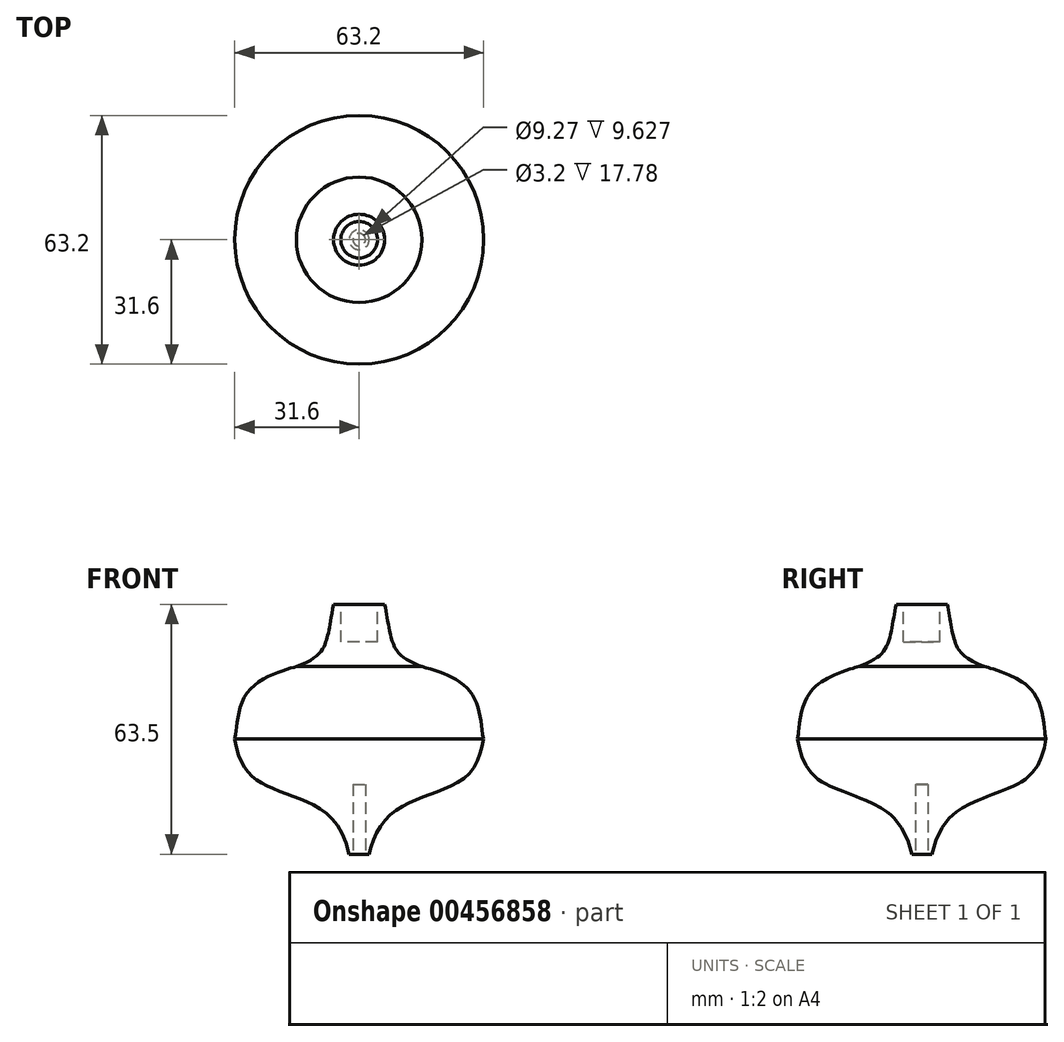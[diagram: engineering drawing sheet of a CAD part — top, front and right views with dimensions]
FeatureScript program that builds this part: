
annotation { "Feature Type Name" : "Feature", "Feature Type Description" : "" }
export const myFeature = defineFeature(function(context is Context, id is Id, definition is map)
    precondition{}
    {
        {
            var Q0;
            Q0=qCreatedBy(makeId("Front.planeOp"),FACE);
            var sketch = newSketch(context, id + "F0", { "sketchPlane" : qUnion([Q0])});
            skLineSegment(sketch, "E0", {"start": v(0, 0) * mm, "end": v(0, 63.5) * mm});
            skLineSegment(sketch, "E1", {"start": v(0, 63.5) * mm, "end": v(6.48, 63.5) * mm});
            skFitSpline(sketch, "E2", {"points": [v(6.48, 63.5) * mm, v(8.36, 54.25) * mm, v(15.93, 47.67) * mm], "startDerivative": vector(5.78, -29.87) * mm, "endDerivative": vector(33.4, -11.93) * mm});
            skLineSegment(sketch, "E3", {"start": v(0, 0) * mm, "end": v(2.54, 0) * mm});
            skFitSpline(sketch, "E4", {"points": [v(15.93, 47.67) * mm, v(28.43, 41) * mm, v(31.6, 29.29) * mm], "startDerivative": vector(13.08, -3.77) * mm, "endDerivative": vector(3.73, -8.35) * mm});
            skFitSpline(sketch, "E5", {"points": [v(2.54, 0) * mm, v(14.6, 13.84) * mm, v(26.07, 18.87) * mm, v(31.6, 29.29) * mm], "startDerivative": vector(15.42, 70.62) * mm, "endDerivative": vector(9.5, 55.34) * mm});
            skSolve(sketch);
        }
        {
            var Q0;
            Q0 = qSketchRegion(id + "F0", true);
            var Q1;
            Q1=sQuery(id+"F0.wireOp",EDGE,"E0");
            revolve(context, id + "F1", {"entities" : qUnion([Q0]), "axis" : qUnion([Q1]), "revolveType" : RevolveType.FULL});
        }
        {
            var Q0;
            Q0=makeQuery(id+"F1.opRevolve","SWEPT_FACE",FACE,{"disambiguationData":[OSD([sQuery(id+"F0.wireOp",EDGE,"E1")])]});
            var sketch = newSketch(context, id + "F2", { "sketchPlane" : qUnion([Q0])});
            skCircle(sketch, "E6", {"center": v(0, 0) * mm, "radius": 4.64 * mm});
            skSolve(sketch);
        }
        {
            var Q0;
            Q0 = qSketchRegion(id + "F2", true);
            extrude(context, id + "F3", {"entities" : qUnion([Q0]), "operationType" : NewBodyOperationType.REMOVE, "oppositeDirection" : true, "depth" : 9.63 * mm});
        }
        {
            var Q0;
            Q0=makeQuery(id+"F1.opRevolve","SWEPT_FACE",FACE,{"disambiguationData":[OSD([sQuery(id+"F0.wireOp",EDGE,"E3")])]});
            var sketch = newSketch(context, id + "F4", { "sketchPlane" : qUnion([Q0])});
            skCircle(sketch, "E7", {"center": v(0, 0) * mm, "radius": 1.6 * mm});
            skSolve(sketch);
        }
        {
            var Q0;
            Q0=makeQuery(id+"F4.imprint","IMPRINT",FACE,{"disambiguationData":[TD([[makeQuery(id+"F4.imprint","IMPRINT",EDGE,{"derivedFrom":sQuery(id+"F4.wireOp",EDGE,"E7")}),1.0]])]});
            extrude(context, id + "F5", {"entities" : qUnion([Q0]), "operationType" : NewBodyOperationType.REMOVE, "oppositeDirection" : true, "depth" : 17.78 * mm});
        }
    });
